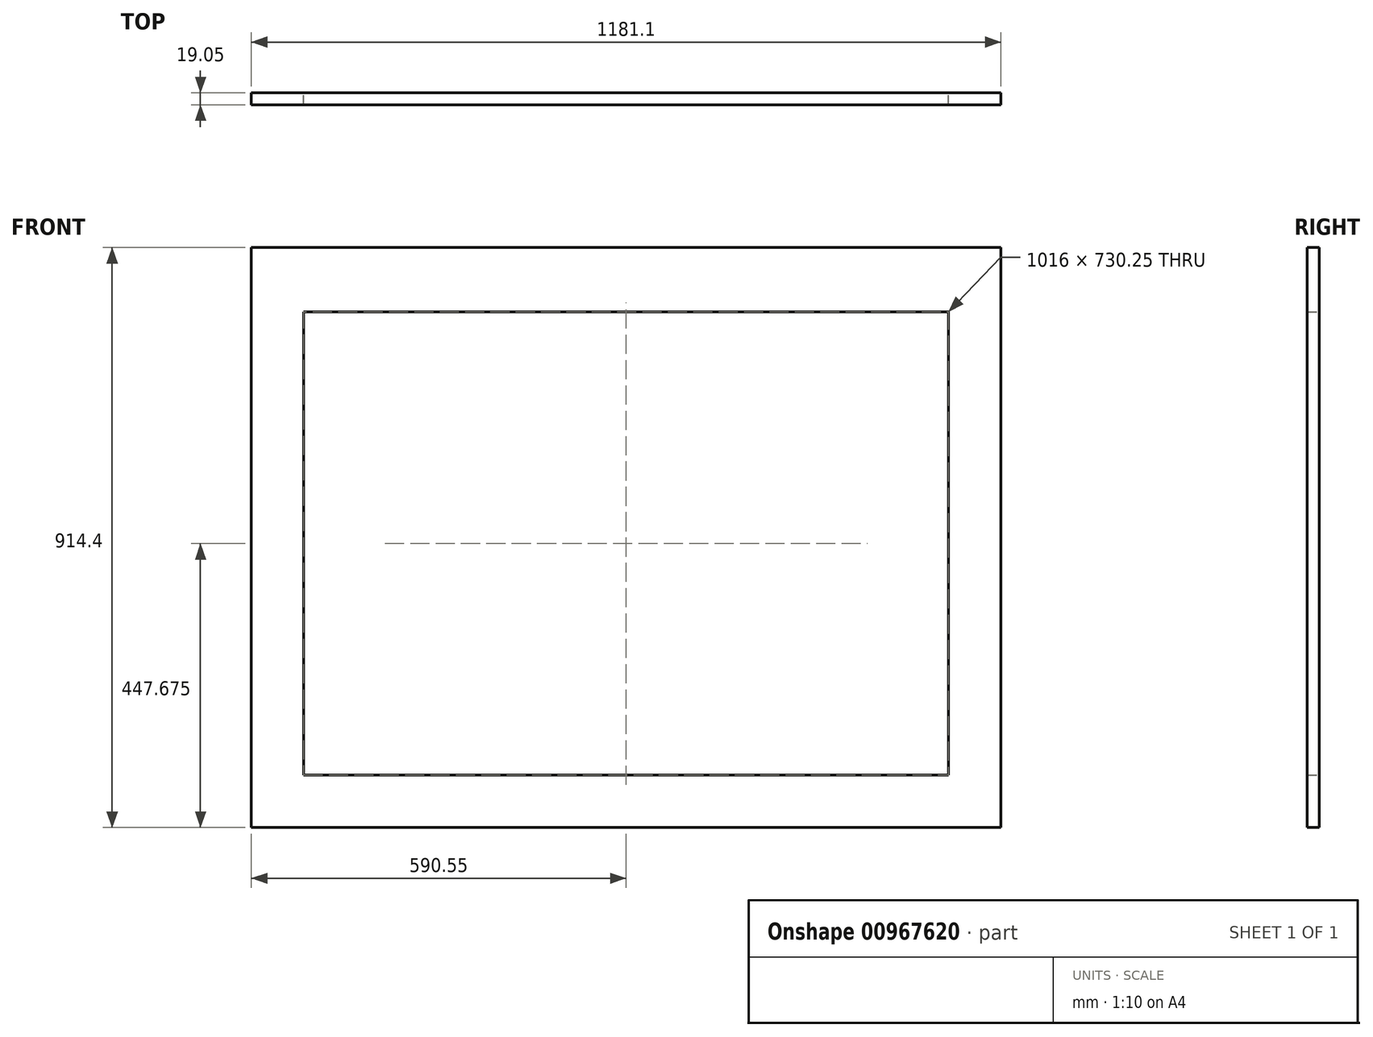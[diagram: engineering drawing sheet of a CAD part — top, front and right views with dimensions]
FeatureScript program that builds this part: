
annotation { "Feature Type Name" : "Feature", "Feature Type Description" : "" }
export const myFeature = defineFeature(function(context is Context, id is Id, definition is map)
    precondition{}
    {
        {
            var Q0;
            Q0=qCreatedBy(makeId("Front.planeOp"),FACE);
            var sketch = newSketch(context, id + "F0", { "sketchPlane" : qUnion([Q0])});
            skLineSegment(sketch, "E0.bottom", {"start": v(590.55, 457.2) * mm, "end": v(-590.55, 457.2) * mm});
            skLineSegment(sketch, "E0.top", {"start": v(590.55, -457.2) * mm, "end": v(-590.55, -457.2) * mm});
            skLineSegment(sketch, "E0.left", {"start": v(590.55, 457.2) * mm, "end": v(590.55, -457.2) * mm});
            skLineSegment(sketch, "E0.right", {"start": v(-590.55, 457.2) * mm, "end": v(-590.55, -457.2) * mm});
            skPoint(sketch, "E0.middle", {"position": v(0, 0) * mm});
            skLineSegment(sketch, "E1.bottom", {"start": v(-508, 355.6) * mm, "end": v(508, 355.6) * mm});
            skLineSegment(sketch, "E1.top", {"start": v(-508, -374.65) * mm, "end": v(508, -374.65) * mm});
            skLineSegment(sketch, "E1.left", {"start": v(-508, 355.6) * mm, "end": v(-508, -374.65) * mm});
            skLineSegment(sketch, "E1.right", {"start": v(508, 355.6) * mm, "end": v(508, -374.65) * mm});
            skSolve(sketch);
        }
        {
            var Q0;
            Q0=makeQuery(id+"F0.imprint","IMPRINT",FACE,{"disambiguationData":[TD([[makeQuery(id+"F0.imprint","IMPRINT",EDGE,{"derivedFrom":sQuery(id+"F0.wireOp",EDGE,"E0.bottom")}),1.0]])]});
            extrude(context, id + "F1", {"entities" : qUnion([Q0]), "depth" : 19.05 * mm, "offsetDistance" : 25.4 * mm});
        }
    });
